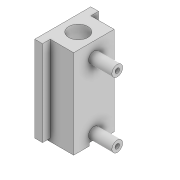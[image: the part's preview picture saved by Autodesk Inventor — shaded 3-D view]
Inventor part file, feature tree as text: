
AUTODESK INVENTOR PART (.ipt)
format: ipt  version: 2022 (Build 260153000, 153)  size: 171,008 bytes
history: native  units: mm
features: extrude x6, sketch x6, projected_geometry x1
ambient origin geometry x8: Origin, YZ Plane, XZ Plane, XY Plane, X Axis, Y Axis, Z Axis, Center Point
bodies: Solid1 (feature_tree)
feature tree (13):
  extrude  "Extrusion1"  Depth=10.0mm
  extrude  "Extrusion2"  Depth=10.0mm
  sketch  "Sketch3"  dims[d4=13.0mm d5=55.0mm d6=0.0mm]
  extrude  "Extrusion3"  Depth=55.0mm TaperAngle=0.0deg
  extrude  "Extrusion6"  Depth=4.0mm
  extrude  "Extrusion7"  Depth=46.0mm
  extrude  "Extrusion8"  Depth=2.0mm
  sketch  "Sketch1"  dims[d0=12.3mm d1=10.0mm]
  sketch  "Sketch2"  dims[d2=10.0mm d3=13.0mm]
  projected_geometry  "Projected Loop1"
  sketch  "Sketch6"  dims[d7=2.9mm d8=4.0mm]
  sketch  "Sketch7"  dims[d9=2.9mm d10=46.0mm]
  sketch  "Sketch8"  dims[d11=13.0mm d12=13.0mm d13=55.0mm d14=0.0mm d15=2.0mm d16=2.0mm d17=15.0mm d18=0.0mm d19=3.2mm d20=3.2mm d21=3.2mm d22=3.2mm d23=4.0mm d24=4.0mm d25=4.0mm d26=4.0mm d31=5.0mm d32=5.0mm d33=0.0mm d34=5.0mm d35=5.0mm d36=0.0mm d37=10.0mm d38=10.0mm d39=2.0mm d40=0.0mm]
